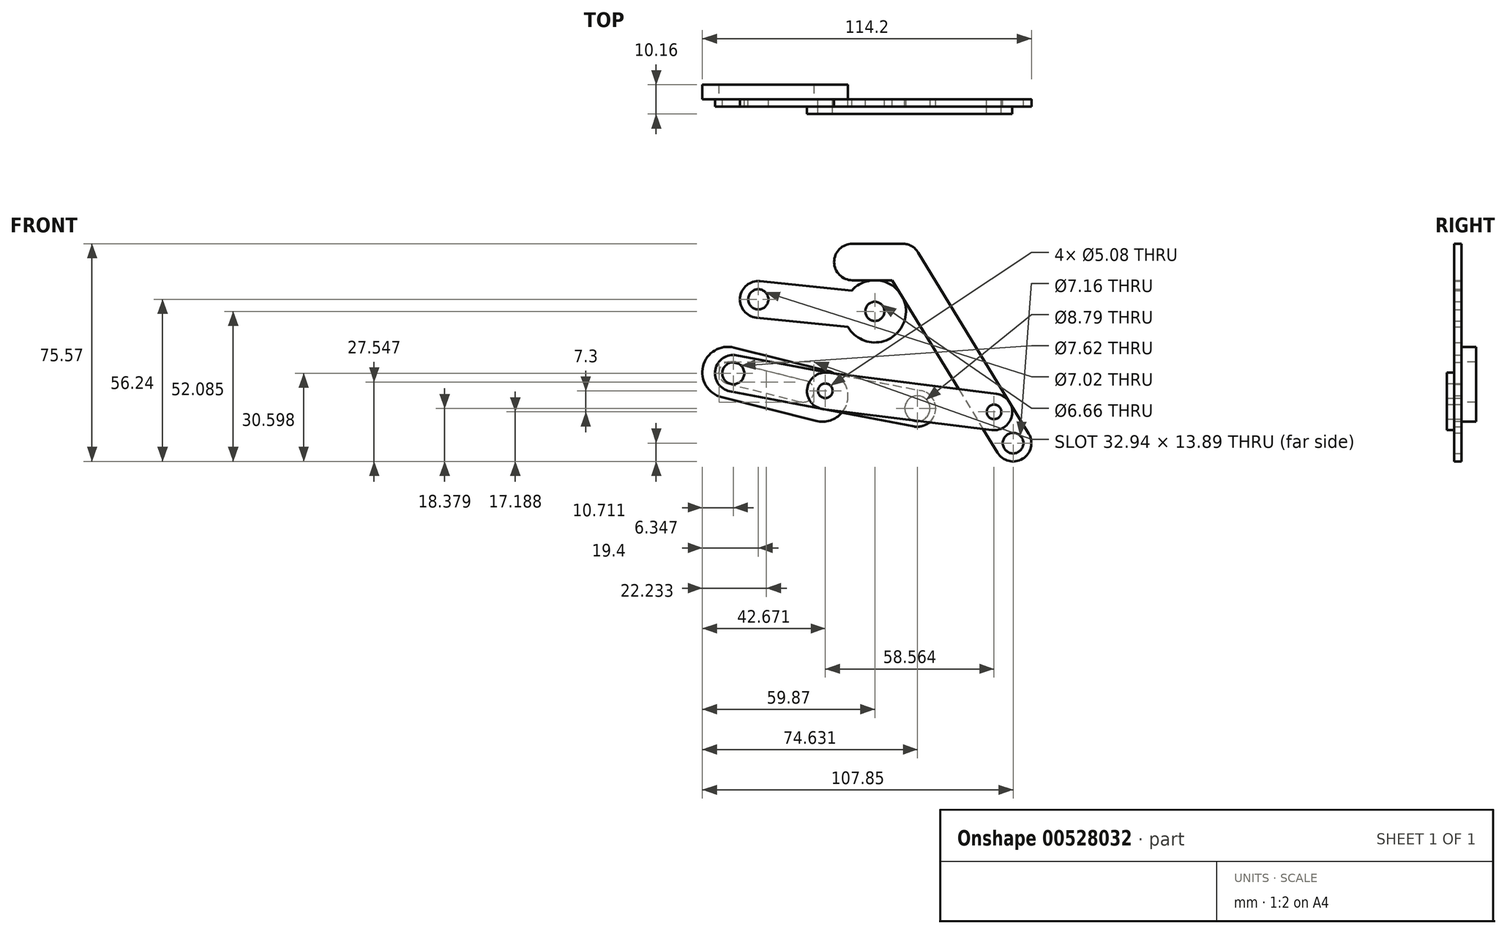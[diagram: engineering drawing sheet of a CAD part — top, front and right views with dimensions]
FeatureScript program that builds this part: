
annotation { "Feature Type Name" : "Feature", "Feature Type Description" : "" }
export const myFeature = defineFeature(function(context is Context, id is Id, definition is map)
    precondition{}
    {
        {
            var Q0;
            Q0=qCreatedBy(makeId("Front.planeOp"),FACE);
            var sketch = newSketch(context, id + "F0", { "sketchPlane" : qUnion([Q0])});
            skLineSegment(sketch, "E0", {"start": v(0, 0) * mm, "end": v(40.47, -4.16) * mm});
            skArc(sketch, "E1.0.startCap", {"start": v(-0.65, -6.32) * mm, "mid": v(-6.32, 0.65) * mm, "end": v(0.65, 6.32) * mm});
            skArc(sketch, "E1.0.endCap", {"start": v(41.12, 2.16) * mm, "mid": v(46.79, -4.8) * mm, "end": v(39.82, -10.47) * mm});
            skLineSegment(sketch, "E1.0.left", {"start": v(0.65, 6.32) * mm, "end": v(41.12, 2.16) * mm});
            skLineSegment(sketch, "E1.0.right", {"start": v(-0.65, -6.32) * mm, "end": v(39.82, -10.47) * mm});
            skCircle(sketch, "E2", {"center": v(0, 0) * mm, "radius": 3.51 * mm});
            skCircle(sketch, "E3", {"center": v(40.47, -4.16) * mm, "radius": 3.33 * mm});
            skLineSegment(sketch, "E4", {"start": v(-8.69, -25.64) * mm, "end": v(55.23, -37.86) * mm});
            skCircle(sketch, "E5", {"center": v(-8.69, -25.64) * mm, "radius": 3.81 * mm});
            skCircle(sketch, "E6", {"center": v(55.23, -37.86) * mm, "radius": 4.4 * mm});
            skArc(sketch, "E7.0.startCap", {"start": v(-9.88, -31.88) * mm, "mid": v(-14.93, -24.45) * mm, "end": v(-7.5, -19.4) * mm});
            skArc(sketch, "E7.0.endCap", {"start": v(56.42, -31.62) * mm, "mid": v(61.47, -39.05) * mm, "end": v(54.04, -44.1) * mm});
            skLineSegment(sketch, "E7.0.left", {"start": v(-7.5, -19.4) * mm, "end": v(56.42, -31.62) * mm});
            skLineSegment(sketch, "E7.0.right", {"start": v(-9.88, -31.88) * mm, "end": v(54.04, -44.1) * mm});
            skCircle(sketch, "E8", {"center": v(23.27, -31.75) * mm, "radius": 2.54 * mm});
            skCircle(sketch, "E9", {"center": v(40.47, -4.16) * mm, "radius": 10.79 * mm});
            skSolve(sketch);
        }
        {
            var Q0;
            Q0 = qSketchRegion(id + "F0", true);
            extrude(context, id + "F1", {"entities" : qUnion([Q0]), "depth" : 2.54 * mm, "offsetDistance" : 25.4 * mm});
        }
        {
            var Q0;
            Q0=qCreatedBy(makeId("Front.planeOp"),FACE);
            var sketch = newSketch(context, id + "F2", { "sketchPlane" : qUnion([Q0])});
            skLineSegment(sketch, "E10", {"start": v(22.27, -33.55) * mm, "end": v(-10.51, -25.36) * mm, "construction": true});
            skArc(sketch, "E11.0.startCap", {"start": v(24.43, -24.93) * mm, "mid": v(30.9, -35.7) * mm, "end": v(20.12, -42.18) * mm});
            skArc(sketch, "E11.0.endCap", {"start": v(-12.67, -33.98) * mm, "mid": v(-19.14, -23.2) * mm, "end": v(-8.36, -16.73) * mm});
            skLineSegment(sketch, "E11.0.left", {"start": v(20.12, -42.18) * mm, "end": v(-12.67, -33.98) * mm});
            skLineSegment(sketch, "E11.0.right", {"start": v(24.43, -24.93) * mm, "end": v(-8.36, -16.73) * mm});
            skLineSegment(sketch, "E12", {"start": v(-9.87, -25.52) * mm, "end": v(15.53, -31.87) * mm});
            skArc(sketch, "E13.0.startCap", {"start": v(-10.8, -29.21) * mm, "mid": v(-13.56, -24.6) * mm, "end": v(-8.94, -21.82) * mm});
            skArc(sketch, "E13.0.endCap", {"start": v(16.46, -28.17) * mm, "mid": v(19.23, -32.8) * mm, "end": v(14.6, -35.56) * mm});
            skLineSegment(sketch, "E13.0.left", {"start": v(-8.94, -21.82) * mm, "end": v(16.46, -28.17) * mm});
            skLineSegment(sketch, "E13.0.right", {"start": v(-10.8, -29.21) * mm, "end": v(14.6, -35.56) * mm});
            skSolve(sketch);
        }
        {
            var Q0;
            Q0 = qSketchRegion(id + "F2", true);
            extrude(context, id + "F3", {"entities" : qUnion([Q0]), "oppositeDirection" : true, "depth" : 5.08 * mm, "offsetDistance" : 25.4 * mm});
        }
        {
            var Q0;
            Q0=qCreatedBy(makeId("Front.planeOp"),FACE);
            var sketch = newSketch(context, id + "F4", { "sketchPlane" : qUnion([Q0])});
            skLineSegment(sketch, "E14", {"start": v(32.68, 12.98) * mm, "end": v(50.09, 12.98) * mm});
            skLineSegment(sketch, "E15", {"start": v(50.09, 12.98) * mm, "end": v(88.45, -49.9) * mm});
            skArc(sketch, "E16.0.startCap", {"start": v(44.67, 9.67) * mm, "mid": v(46.78, 18.4) * mm, "end": v(55.5, 16.29) * mm});
            skArc(sketch, "E16.0.endCap", {"start": v(93.87, -46.59) * mm, "mid": v(91.76, -55.31) * mm, "end": v(83.03, -53.2) * mm});
            skLineSegment(sketch, "E16.0.left", {"start": v(55.5, 16.29) * mm, "end": v(93.87, -46.59) * mm});
            skLineSegment(sketch, "E16.0.right", {"start": v(44.67, 9.67) * mm, "end": v(83.03, -53.2) * mm});
            skArc(sketch, "E16.1.startCap", {"start": v(32.68, 6.63) * mm, "mid": v(26.33, 12.98) * mm, "end": v(32.68, 19.33) * mm});
            skArc(sketch, "E16.1.endCap", {"start": v(50.09, 19.33) * mm, "mid": v(56.44, 12.98) * mm, "end": v(50.09, 6.63) * mm});
            skLineSegment(sketch, "E16.1.left", {"start": v(32.68, 19.33) * mm, "end": v(50.09, 19.33) * mm});
            skLineSegment(sketch, "E16.1.right", {"start": v(32.68, 6.63) * mm, "end": v(50.09, 6.63) * mm});
            skCircle(sketch, "E17", {"center": v(81.84, -39.05) * mm, "radius": 2.54 * mm});
            skCircle(sketch, "E18", {"center": v(88.45, -49.9) * mm, "radius": 3.58 * mm});
            skSolve(sketch);
        }
        {
            var Q0;
            Q0 = qSketchRegion(id + "F4", true);
            extrude(context, id + "F5", {"entities" : qUnion([Q0]), "depth" : 2.54 * mm, "offsetDistance" : 25.4 * mm});
        }
        {
            var Q0;
            Q0=makeQuery(id+"F1.opExtrude","CAP_FACE",FACE,{"disambiguationData":[OSD([sQuery(id+"F0.wireOp",EDGE,"E5"),sQuery(id+"F0.wireOp",EDGE,"E6"),sQuery(id+"F0.wireOp",EDGE,"E7.0.startCap"),sQuery(id+"F0.wireOp",EDGE,"E7.0.endCap"),sQuery(id+"F0.wireOp",EDGE,"E7.0.left"),sQuery(id+"F0.wireOp",EDGE,"E7.0.right")])],"isStart":false});
            var sketch = newSketch(context, id + "F6", { "sketchPlane" : qUnion([Q0])});
            skLineSegment(sketch, "E19", {"start": v(23.27, -31.75) * mm, "end": v(81.84, -39.05) * mm});
            skCircle(sketch, "E20.0", {"center": v(23.27, -31.75) * mm, "radius": 2.54 * mm});
            skCircle(sketch, "E20.1", {"center": v(81.84, -39.05) * mm, "radius": 2.54 * mm});
            skArc(sketch, "E21.0.startCap", {"start": v(22.49, -38.05) * mm, "mid": v(16.97, -30.97) * mm, "end": v(24.06, -25.45) * mm});
            skArc(sketch, "E21.0.endCap", {"start": v(82.62, -32.75) * mm, "mid": v(88.14, -39.84) * mm, "end": v(81.05, -45.35) * mm});
            skLineSegment(sketch, "E21.0.left", {"start": v(24.06, -25.45) * mm, "end": v(82.62, -32.75) * mm});
            skLineSegment(sketch, "E21.0.right", {"start": v(22.49, -38.05) * mm, "end": v(81.05, -45.35) * mm});
            skSolve(sketch);
        }
        {
            var Q0;
            Q0 = qSketchRegion(id + "F6", true);
            extrude(context, id + "F7", {"entities" : qUnion([Q0]), "depth" : 2.54 * mm, "offsetDistance" : 25.4 * mm});
        }
    });
